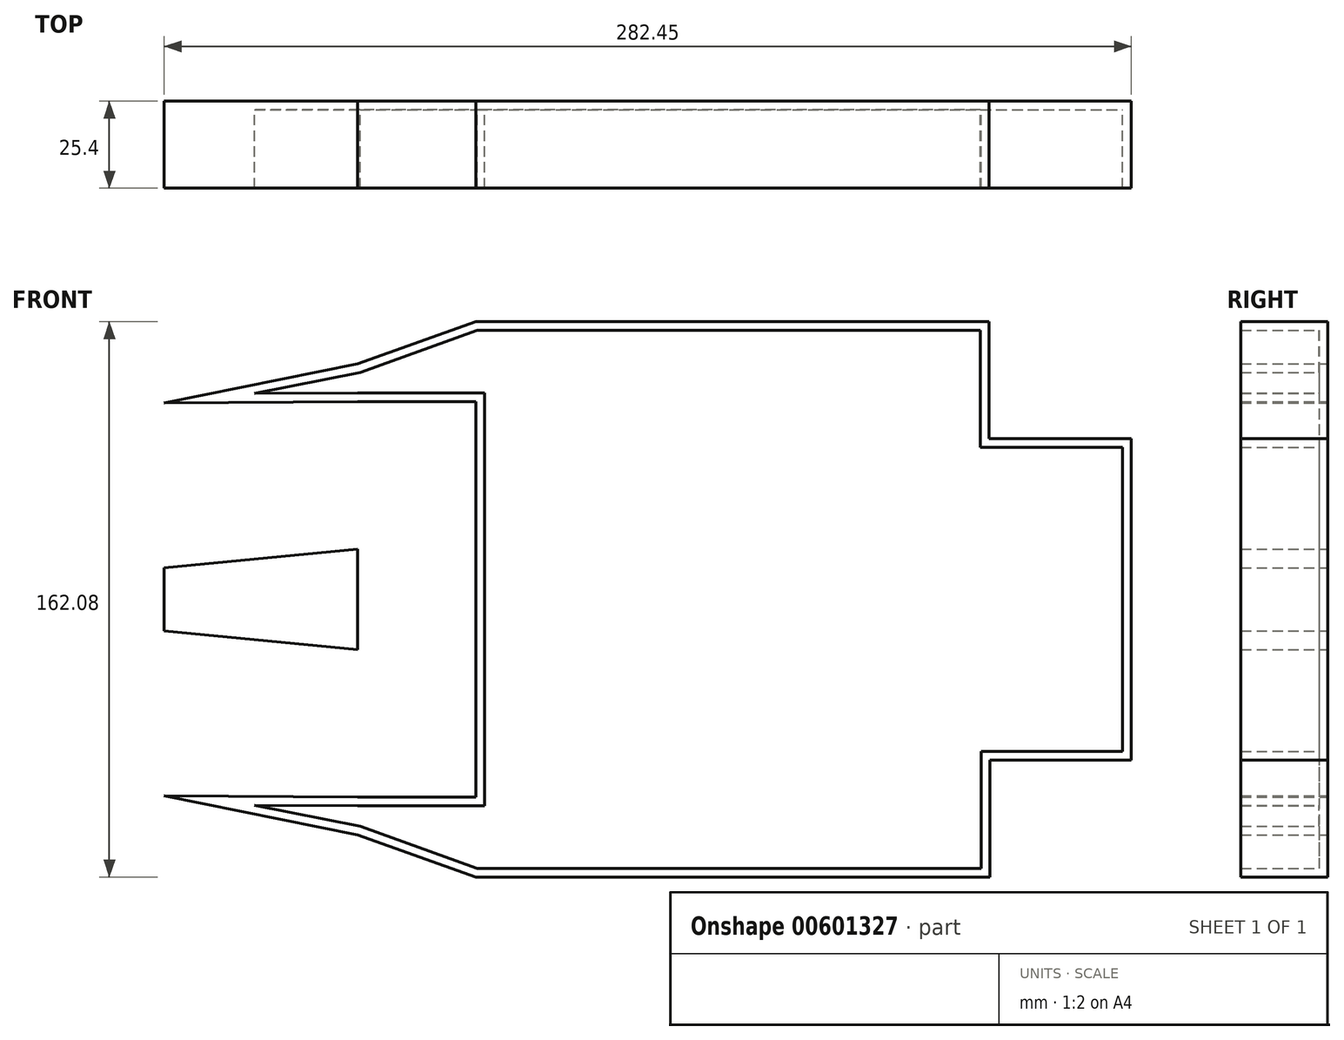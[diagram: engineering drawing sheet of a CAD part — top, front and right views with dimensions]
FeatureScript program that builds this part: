
annotation { "Feature Type Name" : "Feature", "Feature Type Description" : "" }
export const myFeature = defineFeature(function(context is Context, id is Id, definition is map)
    precondition{}
    {
        {
            var Q0;
            Q0=qCreatedBy(makeId("Front.planeOp"),FACE);
            var sketch = newSketch(context, id + "F0", { "sketchPlane" : qUnion([Q0])});
            skLineSegment(sketch, "E0.bottom", {"start": v(0, 81.04) * mm, "end": v(99.88, 81.04) * mm});
            skLineSegment(sketch, "E1.left", {"start": v(99.88, 0) * mm, "end": v(99.88, -19.05) * mm});
            skLineSegment(sketch, "E2.bottom", {"start": v(0, 81.04) * mm, "end": v(-49.95, 81.04) * mm});
            skLineSegment(sketch, "E3.bottom", {"start": v(-49.95, 57.75) * mm, "end": v(-84.45, 57.75) * mm});
            skLineSegment(sketch, "E4", {"start": v(-84.45, 68.74) * mm, "end": v(-49.95, 81.04) * mm});
            skLineSegment(sketch, "E5", {"start": v(-84.45, 68.74) * mm, "end": v(-84.45, 57.75) * mm});
            skLineSegment(sketch, "E6", {"start": v(0, 0) * mm, "end": v(-189.85, 0) * mm, "construction": true});
            skLineSegment(sketch, "E7.MirrorCS", {"start": v(-49.95, -57.75) * mm, "end": v(-84.45, -57.75) * mm});
            skLineSegment(sketch, "E8.MirrorCS", {"start": v(-84.45, -68.74) * mm, "end": v(-49.95, -81.04) * mm});
            skLineSegment(sketch, "E9.MirrorCS", {"start": v(-84.45, -68.74) * mm, "end": v(-84.45, -57.75) * mm});
            skLineSegment(sketch, "E10.bottom", {"start": v(-84.45, 57.75) * mm, "end": v(-49.95, 57.75) * mm});
            skLineSegment(sketch, "E10.top", {"start": v(-84.45, -57.75) * mm, "end": v(-49.95, -57.75) * mm});
            skLineSegment(sketch, "E10.left", {"start": v(-84.45, 57.75) * mm, "end": v(-84.45, -57.75) * mm});
            skLineSegment(sketch, "E11", {"start": v(-84.45, 68.74) * mm, "end": v(-140.94, 57.37) * mm});
            skLineSegment(sketch, "E12", {"start": v(-140.94, 57.37) * mm, "end": v(-84.45, 57.75) * mm});
            skLineSegment(sketch, "E13.MirrorCS", {"start": v(-140.94, -57.37) * mm, "end": v(-84.45, -57.75) * mm});
            skLineSegment(sketch, "E14.MirrorCS", {"start": v(-84.45, -68.74) * mm, "end": v(-140.94, -57.37) * mm});
            skLineSegment(sketch, "E15", {"start": v(-49.95, 81.04) * mm, "end": v(-49.95, -81.04) * mm});
            skLineSegment(sketch, "E16", {"start": v(-49.95, -81.04) * mm, "end": v(100.18, -81.04) * mm});
            skLineSegment(sketch, "E17", {"start": v(0, 81.04) * mm, "end": v(0, -81.04) * mm});
            skLineSegment(sketch, "E18", {"start": v(99.88, 81.04) * mm, "end": v(100.18, -81.04) * mm});
            skPoint(sketch, "E19", {"position": v(-140.94, 9.22) * mm});
            skPoint(sketch, "E20.MirrorP", {"position": v(-140.94, -9.22) * mm});
            skLineSegment(sketch, "E21", {"start": v(-140.94, 9.22) * mm, "end": v(-140.94, -9.22) * mm});
            skLineSegment(sketch, "E22", {"start": v(-140.94, -9.22) * mm, "end": v(-84.45, -14.66) * mm});
            skLineSegment(sketch, "E23.MirrorCS", {"start": v(-140.94, 9.22) * mm, "end": v(-84.45, 14.66) * mm});
            skLineSegment(sketch, "E24.top", {"start": v(99.88, 46.89) * mm, "end": v(141.5, 46.89) * mm});
            skLineSegment(sketch, "E24.left", {"start": v(99.88, 0) * mm, "end": v(99.88, 46.89) * mm});
            skLineSegment(sketch, "E24.right", {"start": v(141.5, 0) * mm, "end": v(141.5, 46.89) * mm});
            skLineSegment(sketch, "E25.MirrorCS", {"start": v(99.88, -46.89) * mm, "end": v(141.5, -46.89) * mm});
            skLineSegment(sketch, "E26.MirrorCS", {"start": v(141.5, 0) * mm, "end": v(141.5, -46.89) * mm});
            skSolve(sketch);
        }
        {
            var Q0;
            {var subQ3=sQuery(id+"F0.wireOp",EDGE,"E10.bottom");Q0=makeQuery(id+"F0.imprint","IMPRINT",FACE,{"disambiguationData":[TD([[makeQuery(id+"F0.imprint","IMPRINT",EDGE,{"derivedFrom":subQ3}),-1.0]])]});}
            var Q1;
            Q1=makeQuery(id+"F0.imprint","IMPRINT",FACE,{"disambiguationData":[TD([[makeQuery(id+"F0.imprint","IMPRINT",EDGE,{"derivedFrom":sQuery(id+"F0.wireOp",EDGE,"E5")}),-1.0]])]});
            var Q2;
            Q2=makeQuery(id+"F0.imprint","IMPRINT",FACE,{"disambiguationData":[TD([[makeQuery(id+"F0.imprint","IMPRINT",EDGE,{"derivedFrom":sQuery(id+"F0.wireOp",EDGE,"E21")}),1.0]])]});
            var Q3;
            Q3=makeQuery(id+"F0.imprint","IMPRINT",FACE,{"disambiguationData":[TD([[makeQuery(id+"F0.imprint","IMPRINT",EDGE,{"derivedFrom":sQuery(id+"F0.wireOp",EDGE,"E9.MirrorCS")}),1.0]])]});
            var Q4;
            {var subQ0=sQuery(id+"F0.wireOp",EDGE,"E8.MirrorCS");Q4=makeQuery(id+"F0.imprint","IMPRINT",FACE,{"disambiguationData":[TD([[makeQuery(id+"F0.imprint","IMPRINT",EDGE,{"derivedFrom":subQ0}),1.0]])]});}
            var Q5;
            {var subQ4=sQuery(id+"F0.wireOp",EDGE,"E2.bottom");Q5=makeQuery(id+"F0.imprint","IMPRINT",FACE,{"disambiguationData":[TD([[makeQuery(id+"F0.imprint","IMPRINT",EDGE,{"derivedFrom":subQ4}),1.0]])]});}
            var Q6;
            {var subQ1=sQuery(id+"F0.wireOp",EDGE,"E0.bottom");Q6=makeQuery(id+"F0.imprint","IMPRINT",FACE,{"disambiguationData":[TD([[makeQuery(id+"F0.imprint","IMPRINT",EDGE,{"derivedFrom":subQ1}),-1.0]])]});}
            var Q7;
            {var subQ4=sQuery(id+"F0.wireOp",EDGE,"E24.right");Q7=makeQuery(id+"F0.imprint","IMPRINT",FACE,{"disambiguationData":[TD([[makeQuery(id+"F0.imprint","IMPRINT",EDGE,{"derivedFrom":subQ4}),1.0]])]});}
            var Q8;
            {var subQ0=sQuery(id+"F0.wireOp",EDGE,"E4");Q8=makeQuery(id+"F0.imprint","IMPRINT",FACE,{"disambiguationData":[TD([[makeQuery(id+"F0.imprint","IMPRINT",EDGE,{"derivedFrom":subQ0}),-1.0]])]});}
            extrude(context, id + "F1", {"entities" : qUnion([Q0, Q1, Q2, Q3, Q4, Q5, Q6, Q7, Q8]), "depth" : 25.4 * mm, "offsetDistance" : 25.4 * mm});
        }
        {
            var Q0;
            Q0=makeQuery(id+"F1.opExtrude","CAP_FACE",FACE,{"disambiguationData":[OSD([sQuery(id+"F0.wireOp",EDGE,"E0.bottom"),sQuery(id+"F0.wireOp",EDGE,"E2.bottom"),sQuery(id+"F0.wireOp",EDGE,"E4"),sQuery(id+"F0.wireOp",EDGE,"E8.MirrorCS"),sQuery(id+"F0.wireOp",EDGE,"E10.left"),sQuery(id+"F0.wireOp",EDGE,"E11"),sQuery(id+"F0.wireOp",EDGE,"E12"),sQuery(id+"F0.wireOp",EDGE,"E13.MirrorCS"),sQuery(id+"F0.wireOp",EDGE,"E14.MirrorCS"),sQuery(id+"F0.wireOp",EDGE,"E16"),sQuery(id+"F0.wireOp",EDGE,"E18"),sQuery(id+"F0.wireOp",EDGE,"E21"),sQuery(id+"F0.wireOp",EDGE,"E22"),sQuery(id+"F0.wireOp",EDGE,"E23.MirrorCS"),sQuery(id+"F0.wireOp",EDGE,"E24.top"),sQuery(id+"F0.wireOp",EDGE,"E24.right"),sQuery(id+"F0.wireOp",EDGE,"E25.MirrorCS"),sQuery(id+"F0.wireOp",EDGE,"E26.MirrorCS")])],"isStart":false});
            shell(context, id + "F2", {"entities" : qUnion([Q0]), "thickness" : 2.54 * mm});
        }
    });
